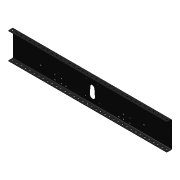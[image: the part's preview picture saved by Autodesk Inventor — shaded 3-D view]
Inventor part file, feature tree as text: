
AUTODESK INVENTOR PART (.ipt)
format: ipt  version: 2015 (Build 190159000, 159)  size: 418,304 bytes
history: native  units: in
note: dims shown in document units (in); Inventor stores cm internally (conversion verified against a paired STEP export)
features: sketch x8, hole x5, other x4, sheet_metal_op x3, fillet x1, extrude x1
ambient origin geometry x8: Origin, YZ Plane, XZ Plane, XY Plane, X Axis, Y Axis, Z Axis, Center Point
bodies: Solid1 (feature_tree)
feature tree (22):
  sheet_metal_op  "Face1"
  sheet_metal_op  "Flange1"
  hole  "Hole1"  [1 undecoded]
  hole  "Hole2"  [1 undecoded]
  hole  "Hole4"  [1 undecoded]
  hole  "Hole5"  [1 undecoded]
  hole  "Hole7"  [1 undecoded]
  fillet  "Fillet1"  Radius=0.09in
  sketch  "Sketch1"  dims[d0=36.0in d1=6.0in]
  other  "Plate1"
  sketch  "Sketch2"  dims[d2=0.09in d3=0.09in]
  other  "Plate2"
  sheet_metal_op  "Bend1"
  sketch  "Sketch3"  dims[d4=0.045in d5=0.18in]
  sketch  "Sketch4"  dims[d6=0.09in d7=1.18in d8=-0.6184in d9=0.09in]
  sketch  "Sketch5"  dims[d10=0.36in d11=0.09in d12=0.09in]
  sketch  "Sketch7"  dims[d13=1.603in d14=0.5in]
  sketch  "Sketch8"  dims[d15=0.625in]
  sketch  "Sketch11"  dims[d16=18.0in d17=36.0in d18=1.625in d19=0.09in d20=0.0in d21=2.5in d22=1.25in d23=3.05in d25=1.176in d26=3.5in d27=1.525in d28=0.206in d29=0.75in d30=0.375in d31=0.25in d32=0.5635in d33=0.09in d34=0.8108in d35=6.3in d36=6.3in d37=1.66in d38=0.266in d39=0.75in d40=0.483in d41=0.25in d42=0.5635in d43=0.09in d44=0.8108in d62=0.5in d63=0.5in d64=14.1732in d66=1.0in d67=0.3937in d69=1.0in d71=0.266in d72=0.75in d73=0.548in d74=0.25in d75=0.5635in d76=0.09in d77=0.8108in d78=12.0in d79=12.0in d80=0.625in d81=4.875in d82=0.266in d83=0.75in d84=0.548in d85=0.25in d86=0.5635in d87=0.09in d88=0.8108in d111=1.5in d112=2.0in d113=9.25in d114=0.25in d115=0.25in d116=0.25in d117=0.25in d118=0.25in d119=0.25in d120=0.25in d121=0.25in d122=0.25in d123=0.25in d124=0.75in d125=0.375in d126=0.25in d127=0.5635in d128=0.09in d129=0.8108in d130=0.125in]
  other  "Cut1"
  other  "Definition1"
  extrude  "Extrusion1"  Depth=0.5in
note: 5 required parameter values undecoded (feature->parameter linkage not recoverable at this tier; creation-order binding heuristic only, values carry confidence <= 0.55)
